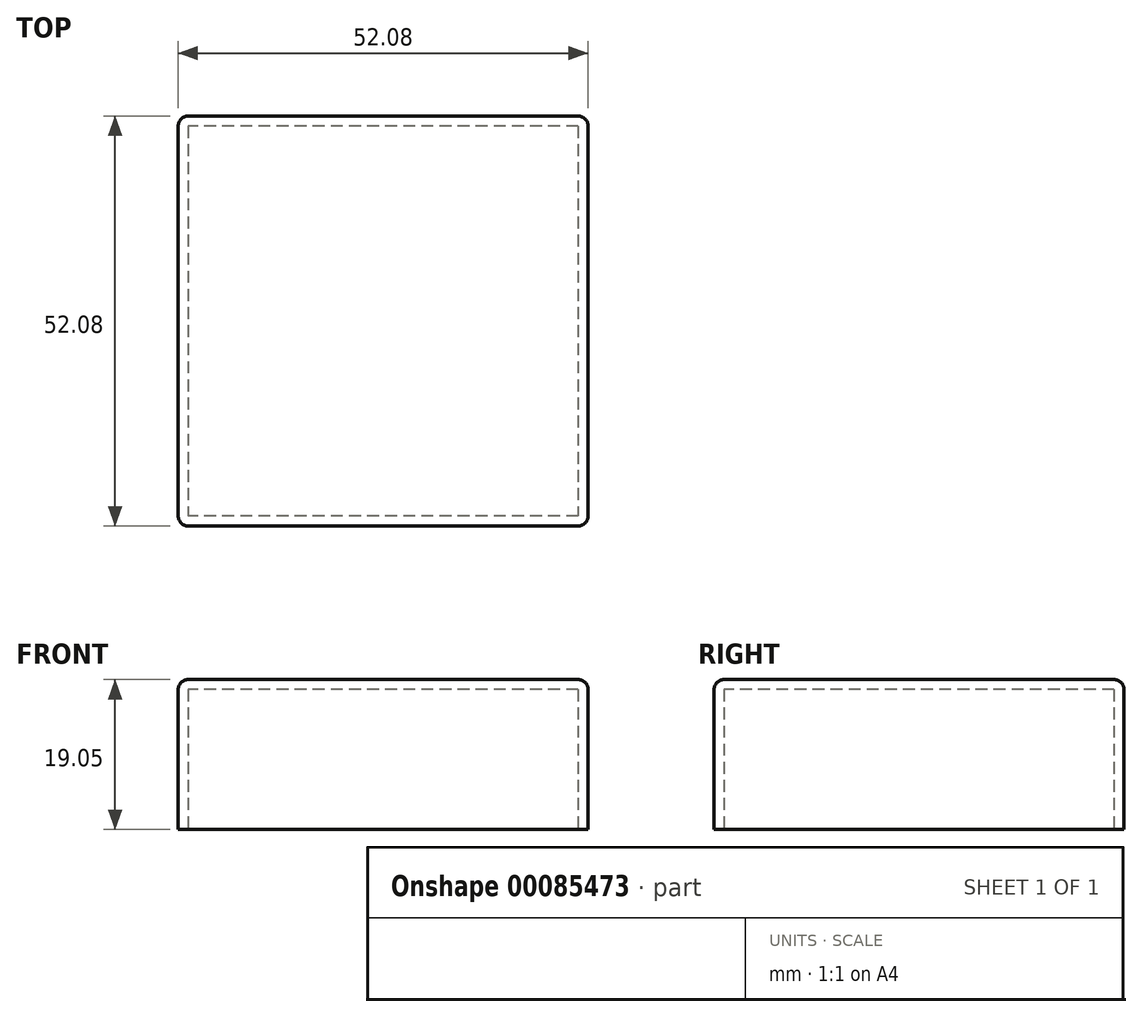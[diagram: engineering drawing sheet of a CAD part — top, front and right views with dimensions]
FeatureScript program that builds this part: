
annotation { "Feature Type Name" : "Feature", "Feature Type Description" : "" }
export const myFeature = defineFeature(function(context is Context, id is Id, definition is map)
    precondition{}
    {
        {
            var Q0;
            Q0=qCreatedBy(makeId("Top.planeOp"),FACE);
            var sketch = newSketch(context, id + "F0", { "sketchPlane" : qUnion([Q0])});
            skLineSegment(sketch, "E0.bottom", {"start": v(26.04, 26.04) * mm, "end": v(-26.04, 26.04) * mm});
            skLineSegment(sketch, "E0.top", {"start": v(26.04, -26.03) * mm, "end": v(-26.04, -26.03) * mm});
            skLineSegment(sketch, "E0.left", {"start": v(26.04, 26.04) * mm, "end": v(26.04, -26.03) * mm});
            skLineSegment(sketch, "E0.right", {"start": v(-26.04, 26.04) * mm, "end": v(-26.04, -26.03) * mm});
            skPoint(sketch, "E0.middle", {"position": v(0, 0) * mm});
            skSolve(sketch);
        }
        {
            var Q0;
            Q0 = qSketchRegion(id + "F0", true);
            extrude(context, id + "F1", {"entities" : qUnion([Q0]), "depth" : 19.05 * mm});
        }
        {
            var Q0;
            Q0=makeQuery(id+"F1.opExtrude","CAP_FACE",FACE,{"disambiguationData":[OSD([sQuery(id+"F0.wireOp",EDGE,"E0.bottom"),sQuery(id+"F0.wireOp",EDGE,"E0.top"),sQuery(id+"F0.wireOp",EDGE,"E0.left"),sQuery(id+"F0.wireOp",EDGE,"E0.right")])],"isStart":true});
            shell(context, id + "F2", {"entities" : qUnion([Q0]), "thickness" : 1.27 * mm});
        }
        {
            var Q0;
            Q0=makeQuery(id+"F1.opExtrude","CAP_EDGE",EDGE,{"disambiguationData":[OSD([sQuery(id+"F0.wireOp",EDGE,"E0.top")])],"isStart":false});
            var Q1;
            Q1=makeQuery(id+"F1.opExtrude","SWEPT_EDGE",EDGE,{"disambiguationData":[OSD([sQuery(id+"F0.wireOp",EDGE,"E0.top"),sQuery(id+"F0.wireOp",EDGE,"E0.right")])]});
            var Q2;
            Q2=makeQuery(id+"F1.opExtrude","CAP_EDGE",EDGE,{"disambiguationData":[OSD([sQuery(id+"F0.wireOp",EDGE,"E0.right")])],"isStart":false});
            var Q3;
            Q3=makeQuery(id+"F1.opExtrude","SWEPT_EDGE",EDGE,{"disambiguationData":[OSD([sQuery(id+"F0.wireOp",EDGE,"E0.bottom"),sQuery(id+"F0.wireOp",EDGE,"E0.right")])]});
            var Q4;
            Q4=makeQuery(id+"F1.opExtrude","CAP_EDGE",EDGE,{"disambiguationData":[OSD([sQuery(id+"F0.wireOp",EDGE,"E0.bottom")])],"isStart":false});
            var Q5;
            Q5=makeQuery(id+"F1.opExtrude","SWEPT_EDGE",EDGE,{"disambiguationData":[OSD([sQuery(id+"F0.wireOp",EDGE,"E0.bottom"),sQuery(id+"F0.wireOp",EDGE,"E0.left")])]});
            var Q6;
            Q6=makeQuery(id+"F1.opExtrude","CAP_EDGE",EDGE,{"disambiguationData":[OSD([sQuery(id+"F0.wireOp",EDGE,"E0.left")])],"isStart":false});
            var Q7;
            Q7=makeQuery(id+"F1.opExtrude","SWEPT_EDGE",EDGE,{"disambiguationData":[OSD([sQuery(id+"F0.wireOp",EDGE,"E0.top"),sQuery(id+"F0.wireOp",EDGE,"E0.left")])]});
            fillet(context, id + "F3", {"entities" : qUnion([Q0, Q1, Q2, Q3, Q4, Q5, Q6, Q7]), "radius" : 1.27 * mm, "tangentPropagation" : true, "allowEdgeOverflow" : false});
        }
    });
